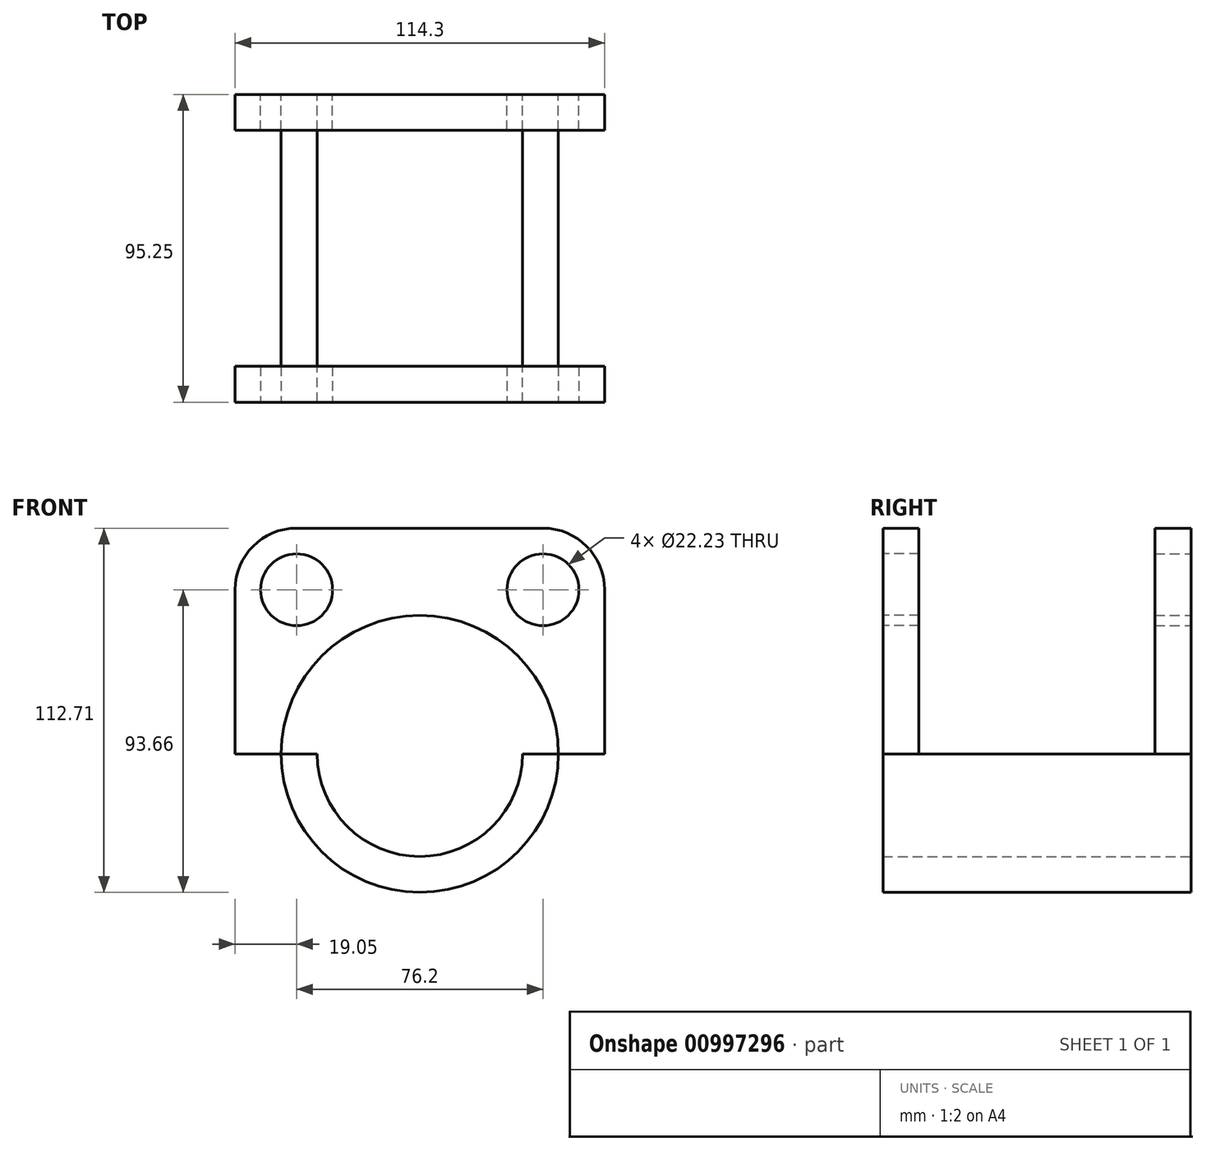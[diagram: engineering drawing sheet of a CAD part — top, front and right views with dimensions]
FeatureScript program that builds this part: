
annotation { "Feature Type Name" : "Feature", "Feature Type Description" : "" }
export const myFeature = defineFeature(function(context is Context, id is Id, definition is map)
    precondition{}
    {
        {
            var Q0;
            Q0=qCreatedBy(makeId("Front.planeOp"),FACE);
            var sketch = newSketch(context, id + "F0", { "sketchPlane" : qUnion([Q0])});
            skCircle(sketch, "E0", {"center": v(0, 0) * mm, "radius": 42.86 * mm});
            skCircle(sketch, "E1", {"center": v(0, 0) * mm, "radius": 31.75 * mm});
            skLineSegment(sketch, "E2", {"start": v(-57.15, 0) * mm, "end": v(57.15, 0) * mm});
            skLineSegment(sketch, "E3.top", {"start": v(-57.15, 69.85) * mm, "end": v(57.15, 69.85) * mm});
            skLineSegment(sketch, "E3.left", {"start": v(-57.15, 0) * mm, "end": v(-57.15, 69.85) * mm});
            skLineSegment(sketch, "E3.right", {"start": v(57.15, 0) * mm, "end": v(57.15, 69.85) * mm});
            skLineSegment(sketch, "E4", {"start": v(-81.94, 50.8) * mm, "end": v(81.92, 50.8) * mm, "construction": true});
            skLineSegment(sketch, "E5.bottom", {"start": v(38.1, 105.82) * mm, "end": v(-38.1, 105.82) * mm, "construction": true});
            skLineSegment(sketch, "E5.left", {"start": v(38.1, 105.82) * mm, "end": v(38.1, -105.82) * mm, "construction": true});
            skLineSegment(sketch, "E5.right", {"start": v(-38.1, 105.82) * mm, "end": v(-38.1, -105.82) * mm, "construction": true});
            skCircle(sketch, "E6", {"center": v(-38.1, 50.8) * mm, "radius": 11.11 * mm});
            skCircle(sketch, "E7", {"center": v(38.1, 50.8) * mm, "radius": 11.11 * mm});
            skLineSegment(sketch, "E8", {"start": v(0, 8.1) * mm, "end": v(0, -10.39) * mm});
            skSolve(sketch);
        }
        {
            var Q0;
            {var subQ0=sQuery(id+"F0.wireOp",EDGE,"E2");var subQ1=sQuery(id+"F0.wireOp",EDGE,"E0");var subQ2=makeQuery(id+"F0.imprint","INTERSECT",VERTEX,{"disambiguationData":[OD(0.0)],"derivedFrom":[subQ1,subQ0]});Q0=makeQuery(id+"F0.imprint","IMPRINT",FACE,{"disambiguationData":[TD([[makeQuery(id+"F0.imprint","IMPRINT",EDGE,{"disambiguationData":[TD([[subQ2,1.0]])],"derivedFrom":subQ1}),1.0]])]});}
            extrude(context, id + "F1", {"entities" : qUnion([Q0]), "depth" : 95.25 * mm, "offsetDistance" : 25.4 * mm});
        }
        {
            var Q0;
            Q0=makeQuery(id+"F0.imprint","IMPRINT",FACE,{"disambiguationData":[TD([[makeQuery(id+"F0.imprint","IMPRINT",EDGE,{"derivedFrom":sQuery(id+"F0.wireOp",EDGE,"E3.top")}),-1.0]])]});
            extrude(context, id + "F2", {"entities" : qUnion([Q0]), "operationType" : NewBodyOperationType.ADD, "depth" : 11.1 * mm, "offsetDistance" : 25.4 * mm});
        }
        {
            var Q0;
            Q0=makeQuery(id+"F1.opExtrude","CAP_FACE",FACE,{"disambiguationData":[OSD([sQuery(id+"F0.wireOp",EDGE,"E0"),sQuery(id+"F0.wireOp",EDGE,"E1"),sQuery(id+"F0.wireOp",EDGE,"E2")])],"isStart":false});
            var sketch = newSketch(context, id + "F3", { "sketchPlane" : qUnion([Q0])});
            skCircle(sketch, "E9", {"center": v(0, 0) * mm, "radius": 42.86 * mm});
            skCircle(sketch, "E10", {"center": v(0, 0) * mm, "radius": 31.75 * mm});
            skLineSegment(sketch, "E11", {"start": v(-57.15, 0) * mm, "end": v(57.15, 0) * mm});
            skLineSegment(sketch, "E12.top", {"start": v(-57.15, 69.85) * mm, "end": v(57.15, 69.85) * mm});
            skLineSegment(sketch, "E12.left", {"start": v(-57.15, 0) * mm, "end": v(-57.15, 69.85) * mm});
            skLineSegment(sketch, "E12.right", {"start": v(57.15, 0) * mm, "end": v(57.15, 69.85) * mm});
            skLineSegment(sketch, "E13.bottom", {"start": v(38.1, 105.82) * mm, "end": v(-38.1, 105.82) * mm, "construction": true});
            skLineSegment(sketch, "E13.left", {"start": v(38.1, 105.82) * mm, "end": v(38.1, -105.82) * mm, "construction": true});
            skLineSegment(sketch, "E13.right", {"start": v(-38.1, 105.82) * mm, "end": v(-38.1, -105.82) * mm, "construction": true});
            skCircle(sketch, "E14", {"center": v(-38.1, 50.8) * mm, "radius": 11.11 * mm});
            skCircle(sketch, "E15", {"center": v(38.1, 50.8) * mm, "radius": 11.11 * mm});
            skSolve(sketch);
        }
        {
            var Q0;
            Q0=makeQuery(id+"F3.imprint","IMPRINT",FACE,{"disambiguationData":[TD([[makeQuery(id+"F3.imprint","IMPRINT",EDGE,{"derivedFrom":sQuery(id+"F3.wireOp",EDGE,"E12.top")}),-1.0]])]});
            extrude(context, id + "F4", {"entities" : qUnion([Q0]), "operationType" : NewBodyOperationType.ADD, "oppositeDirection" : true, "depth" : 11.1 * mm, "offsetDistance" : 25.4 * mm});
        }
        {
            var Q0;
            Q0=makeQuery(id+"F4.opExtrude","SWEPT_EDGE",EDGE,{"disambiguationData":[OSD([sQuery(id+"F3.wireOp",EDGE,"E12.top"),sQuery(id+"F3.wireOp",EDGE,"E12.right")])]});
            var Q1;
            Q1=makeQuery(id+"F2.opExtrude","SWEPT_EDGE",EDGE,{"disambiguationData":[OSD([sQuery(id+"F0.wireOp",EDGE,"E3.top"),sQuery(id+"F0.wireOp",EDGE,"E3.left")])]});
            var Q2;
            Q2=makeQuery(id+"F4.opExtrude","SWEPT_EDGE",EDGE,{"disambiguationData":[OSD([sQuery(id+"F3.wireOp",EDGE,"E12.top"),sQuery(id+"F3.wireOp",EDGE,"E12.left")])]});
            var Q3;
            Q3=makeQuery(id+"F2.opExtrude","SWEPT_EDGE",EDGE,{"disambiguationData":[OSD([sQuery(id+"F0.wireOp",EDGE,"E3.top"),sQuery(id+"F0.wireOp",EDGE,"E3.right")])]});
            fillet(context, id + "F5", {"entities" : qUnion([Q0, Q1, Q2, Q3]), "radius" : 19.05 * mm, "tangentPropagation" : true, "allowEdgeOverflow" : false});
        }
    });
